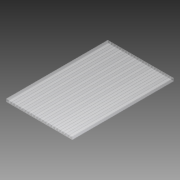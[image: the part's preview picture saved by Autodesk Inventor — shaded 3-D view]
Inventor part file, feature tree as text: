
AUTODESK INVENTOR PART (.ipt)
format: ipt  version: 2012 (Build 160160000, 160)  size: 168,448 bytes
history: native  units: in
note: dims shown in document units (in); Inventor stores cm internally (conversion verified against a paired STEP export)
features: other x3, sketch x1
ambient origin geometry x8: Origin, YZ Plane, XZ Plane, XY Plane, X Axis, Y Axis, Z Axis, Center Point
bodies: Solid1 (feature_tree)
feature tree (4):
  other  "8 ball polycarb side.ipt"
  other  "Solid1::8 ball polycarb side.ipt"
  sketch  "Sketch1"  dims[d0=0.3937in]
  other  "TaggingFeature1"
